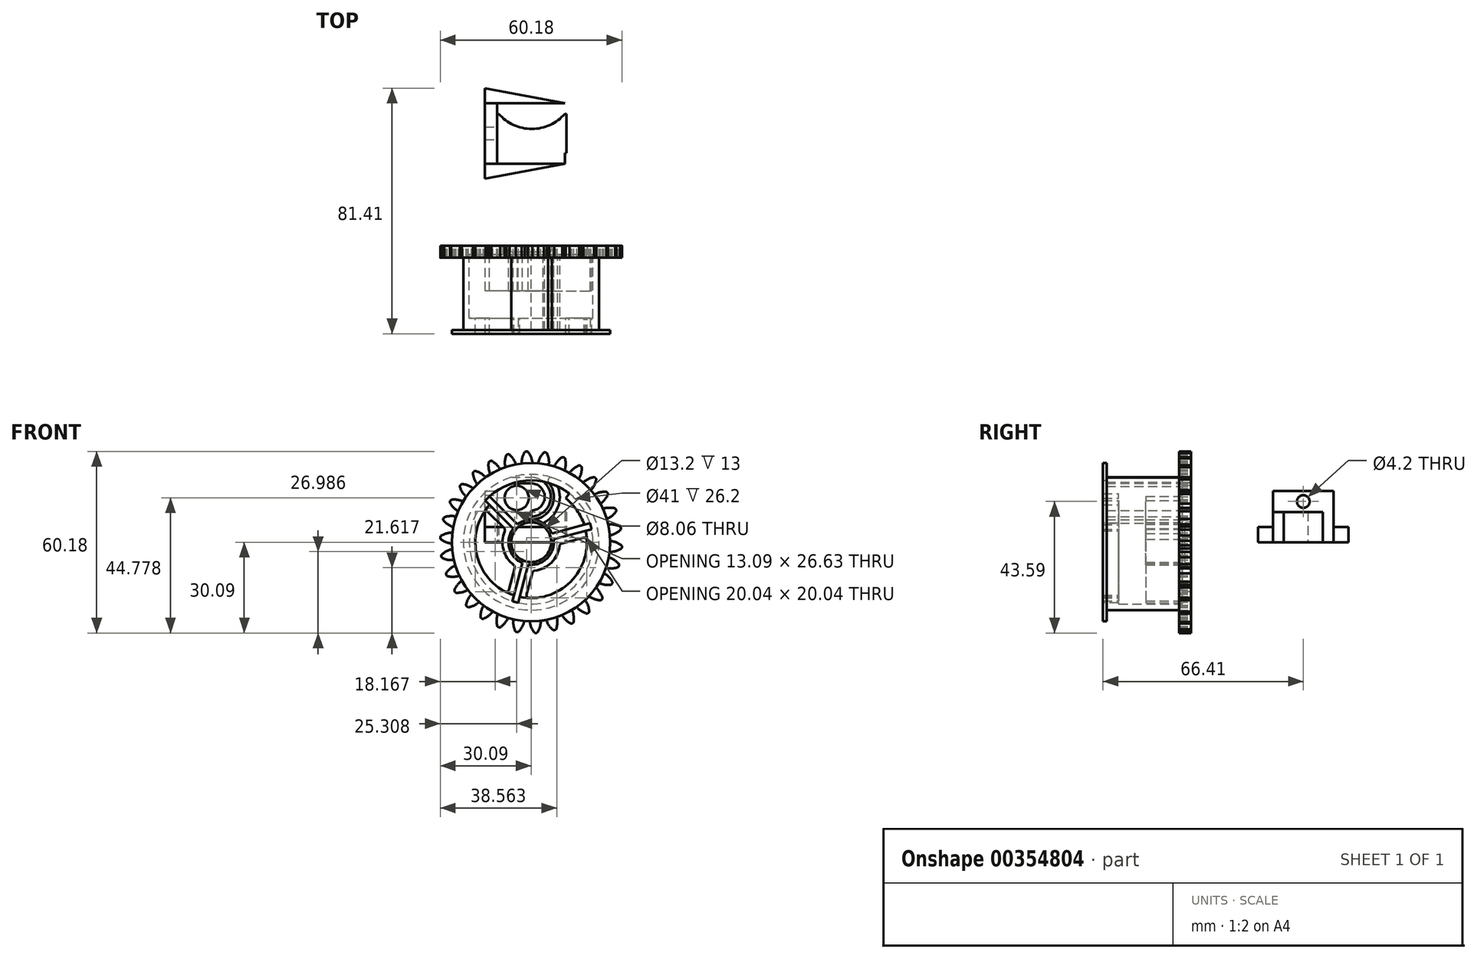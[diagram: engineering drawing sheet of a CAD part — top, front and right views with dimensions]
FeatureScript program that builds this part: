
annotation { "Feature Type Name" : "Feature", "Feature Type Description" : "" }
export const myFeature = defineFeature(function(context is Context, id is Id, definition is map)
    precondition{}
    {
        {
            var Q0;
            Q0=qCreatedBy(makeId("Front.planeOp"),FACE);
            var sketch = newSketch(context, id + "F0", { "sketchPlane" : qUnion([Q0])});
            skCircle(sketch, "E0", {"center": v(0, 0) * mm, "radius": 26.25 * mm});
            skCircle(sketch, "E1", {"center": v(0, 0) * mm, "radius": 30 * mm, "construction": true});
            skCircle(sketch, "E2", {"center": v(0, 0) * mm, "radius": 28.12 * mm, "construction": true});
            skLineSegment(sketch, "E3", {"start": v(0, 0) * mm, "end": v(0, 53.52) * mm, "construction": true});
            skLineSegment(sketch, "E4", {"start": v(0, 0) * mm, "end": v(-2.07, 39.41) * mm, "construction": true});
            skLineSegment(sketch, "E5", {"start": v(0, 28.12) * mm, "end": v(-31.73, 28.12) * mm, "construction": true});
            skLineSegment(sketch, "E6", {"start": v(0, 28.13) * mm, "end": v(-33.86, 15.8) * mm, "construction": true});
            skCircle(sketch, "E7", {"center": v(0, 28.12) * mm, "radius": 7.03 * mm, "construction": true});
            skCircle(sketch, "E8", {"center": v(0, 0) * mm, "radius": 26.43 * mm, "construction": true});
            skCircle(sketch, "E9", {"center": v(-6.56, 25.6) * mm, "radius": 7.03 * mm, "construction": true});
            skArc(sketch, "E10", {"start": v(0.44, 26.25) * mm, "mid": v(-0.04, 28.22) * mm, "end": v(-1.06, 29.98) * mm});
            skCircle(sketch, "E11.MirrorC", {"center": v(3.85, 26.15) * mm, "radius": 7.03 * mm, "construction": true});
            skArc(sketch, "E12.MirrorCS", {"start": v(-3.18, 26.06) * mm, "mid": v(-2.91, 28.07) * mm, "end": v(-2.08, 29.93) * mm});
            skArc(sketch, "E13", {"start": v(-1.06, 29.98) * mm, "mid": v(-1.58, 30.1) * mm, "end": v(-2.08, 29.93) * mm});
            skCircle(sketch, "E14", {"center": v(0, 0) * mm, "radius": 6.6 * mm});
            skCircle(sketch, "E15", {"center": v(0, 0) * mm, "radius": 7.5 * mm});
            skCircle(sketch, "E16", {"center": v(0, 0) * mm, "radius": 22.5 * mm});
            skCircle(sketch, "E17", {"center": v(0, 0) * mm, "radius": 20.5 * mm});
            skArc(sketch, "E18", {"start": v(0, 7.5) * mm, "mid": v(7.5, 15) * mm, "end": v(0, 22.5) * mm});
            skArc(sketch, "E19.0", {"start": v(0, 8.5) * mm, "mid": v(6.5, 15) * mm, "end": v(0, 21.5) * mm});
            skArc(sketch, "E20.0", {"start": v(0, 5.5) * mm, "mid": v(9.5, 15) * mm, "end": v(0, 24.5) * mm});
            skArc(sketch, "E21.0", {"start": v(0, 10.5) * mm, "mid": v(4.5, 15) * mm, "end": v(0, 19.5) * mm});
            skLineSegment(sketch, "E22", {"start": v(0, 19.5) * mm, "end": v(-6.32, 19.5) * mm});
            skLineSegment(sketch, "E23", {"start": v(0, 21.5) * mm, "end": v(-6.63, 21.5) * mm});
            skLineSegment(sketch, "E24", {"start": v(0, 10.5) * mm, "end": v(0, 8.5) * mm});
            skCircle(sketch, "E25", {"center": v(0, 0) * mm, "radius": 10 * mm});
            skLineSegment(sketch, "E26", {"start": v(-5.3, 5.3) * mm, "end": v(-14.5, 14.5) * mm, "construction": true});
            skLineSegment(sketch, "E27.0", {"start": v(-4.55, 5.96) * mm, "end": v(-13.79, 15.2) * mm});
            skLineSegment(sketch, "E28.0", {"start": v(-5.96, 4.55) * mm, "end": v(-15.2, 13.79) * mm});
            skLineSegment(sketch, "E29.1.0", {"start": v(-2.89, -6.92) * mm, "end": v(-6.27, -19.54) * mm});
            skLineSegment(sketch, "E29.1.1", {"start": v(-0.96, -7.44) * mm, "end": v(-4.34, -20.06) * mm});
            skLineSegment(sketch, "E29.2.0", {"start": v(7.44, 0.96) * mm, "end": v(20.06, 4.34) * mm});
            skLineSegment(sketch, "E29.2.1", {"start": v(6.92, 2.89) * mm, "end": v(19.54, 6.27) * mm});
            skPoint(sketch, "E30.orphan", {"position": v(-4.6, 6.01) * mm});
            skPoint(sketch, "E31.orphan", {"position": v(-6.01, 4.6) * mm});
            skPoint(sketch, "E32.orphan", {"position": v(-2.9, -6.99) * mm});
            skPoint(sketch, "E33.orphan", {"position": v(-0.98, -7.5) * mm});
            skPoint(sketch, "E34.orphan", {"position": v(7.5, 0.98) * mm});
            skPoint(sketch, "E35.orphan", {"position": v(6.99, 2.9) * mm});
            skArc(sketch, "E36", {"start": v(7.05, 21.37) * mm, "mid": v(5.74, 21) * mm, "end": v(5.9, 19.63) * mm});
            skSolve(sketch);
        }
        {
            var Q0;
            {var subQ0=sQuery(id+"F0.wireOp",EDGE,"E10");Q0=makeQuery(id+"F0.imprint","IMPRINT",FACE,{"disambiguationData":[TD([[makeQuery(id+"F0.imprint","IMPRINT",EDGE,{"derivedFrom":subQ0}),1.0]])]});}
            var Q1;
            {var subQ4=sQuery(id+"F0.wireOp",EDGE,"E0");var subQ5=makeQuery(id+"F0.imprint","INTERSECT",VERTEX,{"derivedFrom":[subQ4,sQuery(id+"F0.wireOp",EDGE,"E10")]});Q1=makeQuery(id+"F0.imprint","IMPRINT",FACE,{"disambiguationData":[TD([[makeQuery(id+"F0.imprint","IMPRINT",EDGE,{"disambiguationData":[TD([[subQ5,-1.0]])],"derivedFrom":subQ4}),1.0]])]});}
            extrude(context, id + "F1", {"entities" : qUnion([Q0, Q1]), "depth" : 4 * mm});
        }
        {
            var Q0;
            Q0=makeQuery(id+"F1.opExtrude","SWEPT_BODY",BODY,{"disambiguationData":[OSD([sQuery(id+"F0.wireOp",EDGE,"E0"),sQuery(id+"F0.wireOp",EDGE,"E10"),sQuery(id+"F0.wireOp",EDGE,"E12.MirrorCS"),sQuery(id+"F0.wireOp",EDGE,"E13")])]});
            var Q1;
            Q1=makeQuery(id+"F1.opExtrude","SWEPT_FACE",FACE,{"disambiguationData":[OSD([sQuery(id+"F0.wireOp",EDGE,"E0")])]});
            circularPattern(context, id + "F2", {"operationType" : NewBodyOperationType.ADD, "entities" : qUnion([Q0]), "axis" : qUnion([Q1]), "angle" : 360 * degree, "instanceCount" : 30, "equalSpace" : true});
        }
        {
            var Q0;
            {var subQ7=sQuery(id+"F0.wireOp",EDGE,"E23");Q0=makeQuery(id+"F0.imprint","IMPRINT",FACE,{"disambiguationData":[TD([[makeQuery(id+"F0.imprint","IMPRINT",EDGE,{"derivedFrom":subQ7}),1.0]])]});}
            var Q1;
            {var subQ0=sQuery(id+"F0.wireOp",EDGE,"E23");Q1=makeQuery(id+"F0.imprint","IMPRINT",FACE,{"disambiguationData":[TD([[makeQuery(id+"F0.imprint","IMPRINT",EDGE,{"derivedFrom":subQ0}),-1.0]])]});}
            var Q2;
            {var subQ0=sQuery(id+"F0.wireOp",EDGE,"E18");var subQ1=sQuery(id+"F0.wireOp",EDGE,"E16");var subQ2=makeQuery(id+"F0.imprint","INTERSECT",VERTEX,{"derivedFrom":[subQ1,subQ0]});Q2=makeQuery(id+"F0.imprint","IMPRINT",FACE,{"disambiguationData":[TD([[makeQuery(id+"F0.imprint","IMPRINT",EDGE,{"disambiguationData":[TD([[subQ2,1.0]])],"derivedFrom":subQ1}),1.0]])]});}
            var Q3;
            {var subQ0=sQuery(id+"F0.wireOp",EDGE,"E20.0");var subQ1=sQuery(id+"F0.wireOp",EDGE,"E17");var subQ2=makeQuery(id+"F0.imprint","INTERSECT",VERTEX,{"derivedFrom":[subQ1,subQ0]});Q3=makeQuery(id+"F0.imprint","IMPRINT",FACE,{"disambiguationData":[TD([[makeQuery(id+"F0.imprint","IMPRINT",EDGE,{"disambiguationData":[TD([[subQ2,-1.0]])],"derivedFrom":subQ1}),1.0]])]});}
            var Q4;
            {var subQ0=sQuery(id+"F0.wireOp",EDGE,"E18");var subQ1=sQuery(id+"F0.wireOp",EDGE,"E17");var subQ2=makeQuery(id+"F0.imprint","INTERSECT",VERTEX,{"derivedFrom":[subQ1,subQ0]});Q4=makeQuery(id+"F0.imprint","IMPRINT",FACE,{"disambiguationData":[TD([[makeQuery(id+"F0.imprint","IMPRINT",EDGE,{"disambiguationData":[TD([[subQ2,-1.0]])],"derivedFrom":subQ1}),1.0]])]});}
            var Q5;
            {var subQ1=sQuery(id+"F0.wireOp",EDGE,"E21.0");Q5=makeQuery(id+"F0.imprint","IMPRINT",FACE,{"disambiguationData":[TD([[makeQuery(id+"F0.imprint","IMPRINT",EDGE,{"derivedFrom":subQ1}),-1.0]])]});}
            var Q6;
            {var subQ1=sQuery(id+"F0.wireOp",EDGE,"E21.0");Q6=makeQuery(id+"F0.imprint","IMPRINT",FACE,{"disambiguationData":[TD([[makeQuery(id+"F0.imprint","IMPRINT",EDGE,{"derivedFrom":subQ1}),1.0]])]});}
            var Q7;
            {var subQ0=sQuery(id+"F0.wireOp",EDGE,"E28.0");var subQ1=sQuery(id+"F0.wireOp",EDGE,"E17");var subQ2=makeQuery(id+"F0.imprint","INTERSECT",VERTEX,{"derivedFrom":[subQ1,subQ0]});Q7=makeQuery(id+"F0.imprint","IMPRINT",FACE,{"disambiguationData":[TD([[makeQuery(id+"F0.imprint","IMPRINT",EDGE,{"disambiguationData":[TD([[subQ2,-1.0]])],"derivedFrom":subQ1}),1.0]])]});}
            var Q8;
            {var subQ10=sQuery(id+"F0.wireOp",EDGE,"E18");var subQ11=sQuery(id+"F0.wireOp",EDGE,"E15");var subQ12=makeQuery(id+"F0.imprint","INTERSECT",VERTEX,{"derivedFrom":[subQ11,subQ10]});Q8=makeQuery(id+"F0.imprint","IMPRINT",FACE,{"disambiguationData":[TD([[makeQuery(id+"F0.imprint","IMPRINT",EDGE,{"disambiguationData":[TD([[subQ12,-1.0]])],"derivedFrom":subQ11}),-1.0]])]});}
            var Q9;
            {var subQ0=sQuery(id+"F0.wireOp",EDGE,"E29.2.0");var subQ1=sQuery(id+"F0.wireOp",EDGE,"E17");var subQ2=makeQuery(id+"F0.imprint","INTERSECT",VERTEX,{"derivedFrom":[subQ1,subQ0]});Q9=makeQuery(id+"F0.imprint","IMPRINT",FACE,{"disambiguationData":[TD([[makeQuery(id+"F0.imprint","IMPRINT",EDGE,{"disambiguationData":[TD([[subQ2,1.0]])],"derivedFrom":subQ1}),1.0]])]});}
            var Q10;
            {var subQ0=sQuery(id+"F0.wireOp",EDGE,"E29.2.1");var subQ1=sQuery(id+"F0.wireOp",EDGE,"E17");var subQ2=makeQuery(id+"F0.imprint","INTERSECT",VERTEX,{"derivedFrom":[subQ1,subQ0]});Q10=makeQuery(id+"F0.imprint","IMPRINT",FACE,{"disambiguationData":[TD([[makeQuery(id+"F0.imprint","IMPRINT",EDGE,{"disambiguationData":[TD([[subQ2,-1.0]])],"derivedFrom":subQ1}),1.0]])]});}
            var Q11;
            {var subQ0=sQuery(id+"F0.wireOp",EDGE,"E29.2.1");var subQ1=sQuery(id+"F0.wireOp",EDGE,"E17");var subQ2=makeQuery(id+"F0.imprint","INTERSECT",VERTEX,{"derivedFrom":[subQ1,subQ0]});Q11=makeQuery(id+"F0.imprint","IMPRINT",FACE,{"disambiguationData":[TD([[makeQuery(id+"F0.imprint","IMPRINT",EDGE,{"disambiguationData":[TD([[subQ2,1.0]])],"derivedFrom":subQ1}),1.0]])]});}
            var Q12;
            {var subQ0=sQuery(id+"F0.wireOp",EDGE,"E18");var subQ1=sQuery(id+"F0.wireOp",EDGE,"E15");var subQ2=makeQuery(id+"F0.imprint","INTERSECT",VERTEX,{"derivedFrom":[subQ1,subQ0]});Q12=makeQuery(id+"F0.imprint","IMPRINT",FACE,{"disambiguationData":[TD([[makeQuery(id+"F0.imprint","IMPRINT",EDGE,{"disambiguationData":[TD([[subQ2,1.0]])],"derivedFrom":subQ1}),-1.0]])]});}
            var Q13;
            Q13=makeQuery(id+"F0.imprint","IMPRINT",FACE,{"disambiguationData":[TD([[makeQuery(id+"F0.imprint","IMPRINT",EDGE,{"derivedFrom":sQuery(id+"F0.wireOp",EDGE,"E14")}),-1.0]])]});
            var Q14;
            {var subQ0=sQuery(id+"F0.wireOp",EDGE,"E24");var subQ1=sQuery(id+"F0.wireOp",EDGE,"E19.0");var subQ2=makeQuery(id+"F0.imprint","INTERSECT",VERTEX,{"derivedFrom":[subQ1,subQ0]});Q14=makeQuery(id+"F0.imprint","IMPRINT",FACE,{"disambiguationData":[TD([[makeQuery(id+"F0.imprint","IMPRINT",EDGE,{"disambiguationData":[TD([[subQ2,-1.0]])],"derivedFrom":subQ1}),1.0]])]});}
            var Q15;
            {var subQ0=sQuery(id+"F0.wireOp",EDGE,"E29.1.0");var subQ1=sQuery(id+"F0.wireOp",EDGE,"E17");var subQ2=makeQuery(id+"F0.imprint","INTERSECT",VERTEX,{"derivedFrom":[subQ1,subQ0]});Q15=makeQuery(id+"F0.imprint","IMPRINT",FACE,{"disambiguationData":[TD([[makeQuery(id+"F0.imprint","IMPRINT",EDGE,{"disambiguationData":[TD([[subQ2,-1.0]])],"derivedFrom":subQ1}),1.0]])]});}
            var Q16;
            {var subQ0=sQuery(id+"F0.wireOp",EDGE,"E27.0");var subQ1=sQuery(id+"F0.wireOp",EDGE,"E17");var subQ2=makeQuery(id+"F0.imprint","INTERSECT",VERTEX,{"derivedFrom":[subQ1,subQ0]});Q16=makeQuery(id+"F0.imprint","IMPRINT",FACE,{"disambiguationData":[TD([[makeQuery(id+"F0.imprint","IMPRINT",EDGE,{"disambiguationData":[TD([[subQ2,-1.0]])],"derivedFrom":subQ1}),1.0]])]});}
            var Q17;
            {var subQ0=sQuery(id+"F0.wireOp",EDGE,"E29.1.0");var subQ1=sQuery(id+"F0.wireOp",EDGE,"E15");var subQ2=makeQuery(id+"F0.imprint","INTERSECT",VERTEX,{"derivedFrom":[subQ1,subQ0]});Q17=makeQuery(id+"F0.imprint","IMPRINT",FACE,{"disambiguationData":[TD([[makeQuery(id+"F0.imprint","IMPRINT",EDGE,{"disambiguationData":[TD([[subQ2,-1.0]])],"derivedFrom":subQ1}),-1.0]])]});}
            var Q18;
            {var subQ0=sQuery(id+"F0.wireOp",EDGE,"E28.0");var subQ1=sQuery(id+"F0.wireOp",EDGE,"E15");var subQ2=makeQuery(id+"F0.imprint","INTERSECT",VERTEX,{"derivedFrom":[subQ1,subQ0]});Q18=makeQuery(id+"F0.imprint","IMPRINT",FACE,{"disambiguationData":[TD([[makeQuery(id+"F0.imprint","IMPRINT",EDGE,{"disambiguationData":[TD([[subQ2,-1.0]])],"derivedFrom":subQ1}),-1.0]])]});}
            var Q19;
            {var subQ0=sQuery(id+"F0.wireOp",EDGE,"E29.1.1");var subQ1=sQuery(id+"F0.wireOp",EDGE,"E15");var subQ2=makeQuery(id+"F0.imprint","INTERSECT",VERTEX,{"derivedFrom":[subQ1,subQ0]});Q19=makeQuery(id+"F0.imprint","IMPRINT",FACE,{"disambiguationData":[TD([[makeQuery(id+"F0.imprint","IMPRINT",EDGE,{"disambiguationData":[TD([[subQ2,-1.0]])],"derivedFrom":subQ1}),-1.0]])]});}
            var Q20;
            {var subQ0=sQuery(id+"F0.wireOp",EDGE,"E27.0");var subQ1=sQuery(id+"F0.wireOp",EDGE,"E15");var subQ2=makeQuery(id+"F0.imprint","INTERSECT",VERTEX,{"derivedFrom":[subQ1,subQ0]});Q20=makeQuery(id+"F0.imprint","IMPRINT",FACE,{"disambiguationData":[TD([[makeQuery(id+"F0.imprint","IMPRINT",EDGE,{"disambiguationData":[TD([[subQ2,-1.0]])],"derivedFrom":subQ1}),-1.0]])]});}
            var Q21;
            {var subQ0=sQuery(id+"F0.wireOp",EDGE,"E29.2.1");var subQ1=sQuery(id+"F0.wireOp",EDGE,"E15");var subQ2=makeQuery(id+"F0.imprint","INTERSECT",VERTEX,{"derivedFrom":[subQ1,subQ0]});Q21=makeQuery(id+"F0.imprint","IMPRINT",FACE,{"disambiguationData":[TD([[makeQuery(id+"F0.imprint","IMPRINT",EDGE,{"disambiguationData":[TD([[subQ2,-1.0]])],"derivedFrom":subQ1}),-1.0]])]});}
            var Q22;
            {var subQ0=sQuery(id+"F0.wireOp",EDGE,"E29.2.0");var subQ1=sQuery(id+"F0.wireOp",EDGE,"E15");var subQ2=makeQuery(id+"F0.imprint","INTERSECT",VERTEX,{"derivedFrom":[subQ1,subQ0]});Q22=makeQuery(id+"F0.imprint","IMPRINT",FACE,{"disambiguationData":[TD([[makeQuery(id+"F0.imprint","IMPRINT",EDGE,{"disambiguationData":[TD([[subQ2,-1.0]])],"derivedFrom":subQ1}),-1.0]])]});}
            var Q23;
            {var subQ0=sQuery(id+"F0.wireOp",EDGE,"E36");var subQ2=sQuery(id+"F0.wireOp",EDGE,"E16");var subQ9=makeQuery(id+"F0.imprint","INTERSECT",VERTEX,{"derivedFrom":[subQ2,subQ0]});Q23=makeQuery(id+"F0.imprint","IMPRINT",FACE,{"disambiguationData":[TD([[makeQuery(id+"F0.imprint","IMPRINT",EDGE,{"disambiguationData":[TD([[subQ9,-1.0]])],"derivedFrom":subQ0}),1.0]])]});}
            extrude(context, id + "F3", {"entities" : qUnion([Q0, Q1, Q2, Q3, Q4, Q5, Q6, Q7, Q8, Q9, Q10, Q11, Q12, Q13, Q14, Q15, Q16, Q17, Q18, Q19, Q20, Q21, Q22, Q23]), "operationType" : NewBodyOperationType.ADD, "depth" : 3 * mm});
        }
        {
            var Q0;
            {var subQ7=sQuery(id+"F0.wireOp",EDGE,"E23");Q0=makeQuery(id+"F0.imprint","IMPRINT",FACE,{"disambiguationData":[TD([[makeQuery(id+"F0.imprint","IMPRINT",EDGE,{"derivedFrom":subQ7}),1.0]])]});}
            var Q1;
            {var subQ1=sQuery(id+"F0.wireOp",EDGE,"E21.0");Q1=makeQuery(id+"F0.imprint","IMPRINT",FACE,{"disambiguationData":[TD([[makeQuery(id+"F0.imprint","IMPRINT",EDGE,{"derivedFrom":subQ1}),-1.0]])]});}
            var Q2;
            {var subQ0=sQuery(id+"F0.wireOp",EDGE,"E20.0");var subQ1=sQuery(id+"F0.wireOp",EDGE,"E17");var subQ2=makeQuery(id+"F0.imprint","INTERSECT",VERTEX,{"derivedFrom":[subQ1,subQ0]});Q2=makeQuery(id+"F0.imprint","IMPRINT",FACE,{"disambiguationData":[TD([[makeQuery(id+"F0.imprint","IMPRINT",EDGE,{"disambiguationData":[TD([[subQ2,-1.0]])],"derivedFrom":subQ1}),1.0]])]});}
            var Q3;
            {var subQ0=sQuery(id+"F0.wireOp",EDGE,"E18");var subQ1=sQuery(id+"F0.wireOp",EDGE,"E15");var subQ2=makeQuery(id+"F0.imprint","INTERSECT",VERTEX,{"derivedFrom":[subQ1,subQ0]});Q3=makeQuery(id+"F0.imprint","IMPRINT",FACE,{"disambiguationData":[TD([[makeQuery(id+"F0.imprint","IMPRINT",EDGE,{"disambiguationData":[TD([[subQ2,1.0]])],"derivedFrom":subQ1}),-1.0]])]});}
            var Q4;
            {var subQ0=sQuery(id+"F0.wireOp",EDGE,"E24");var subQ1=sQuery(id+"F0.wireOp",EDGE,"E19.0");var subQ2=makeQuery(id+"F0.imprint","INTERSECT",VERTEX,{"derivedFrom":[subQ1,subQ0]});Q4=makeQuery(id+"F0.imprint","IMPRINT",FACE,{"disambiguationData":[TD([[makeQuery(id+"F0.imprint","IMPRINT",EDGE,{"disambiguationData":[TD([[subQ2,-1.0]])],"derivedFrom":subQ1}),1.0]])]});}
            var Q5;
            {var subQ0=sQuery(id+"F0.wireOp",EDGE,"E36");var subQ2=sQuery(id+"F0.wireOp",EDGE,"E16");var subQ9=makeQuery(id+"F0.imprint","INTERSECT",VERTEX,{"derivedFrom":[subQ2,subQ0]});Q5=makeQuery(id+"F0.imprint","IMPRINT",FACE,{"disambiguationData":[TD([[makeQuery(id+"F0.imprint","IMPRINT",EDGE,{"disambiguationData":[TD([[subQ9,-1.0]])],"derivedFrom":subQ0}),1.0]])]});}
            extrude(context, id + "F4", {"entities" : qUnion([Q0, Q1, Q2, Q3, Q4, Q5]), "operationType" : NewBodyOperationType.ADD, "depth" : 28 * mm});
        }
        {
            var Q0;
            {var subQ0=sQuery(id+"F0.wireOp",EDGE,"E29.2.1");var subQ1=sQuery(id+"F0.wireOp",EDGE,"E17");var subQ2=makeQuery(id+"F0.imprint","INTERSECT",VERTEX,{"derivedFrom":[subQ1,subQ0]});Q0=makeQuery(id+"F0.imprint","IMPRINT",FACE,{"disambiguationData":[TD([[makeQuery(id+"F0.imprint","IMPRINT",EDGE,{"disambiguationData":[TD([[subQ2,1.0]])],"derivedFrom":subQ1}),1.0]])]});}
            var Q1;
            {var subQ0=sQuery(id+"F0.wireOp",EDGE,"E29.2.0");var subQ1=sQuery(id+"F0.wireOp",EDGE,"E15");var subQ2=makeQuery(id+"F0.imprint","INTERSECT",VERTEX,{"derivedFrom":[subQ1,subQ0]});Q1=makeQuery(id+"F0.imprint","IMPRINT",FACE,{"disambiguationData":[TD([[makeQuery(id+"F0.imprint","IMPRINT",EDGE,{"disambiguationData":[TD([[subQ2,-1.0]])],"derivedFrom":subQ1}),-1.0]])]});}
            var Q2;
            Q2=makeQuery(id+"F0.imprint","IMPRINT",FACE,{"disambiguationData":[TD([[makeQuery(id+"F0.imprint","IMPRINT",EDGE,{"derivedFrom":sQuery(id+"F0.wireOp",EDGE,"E14")}),-1.0]])]});
            var Q3;
            {var subQ0=sQuery(id+"F0.wireOp",EDGE,"E29.1.0");var subQ1=sQuery(id+"F0.wireOp",EDGE,"E15");var subQ2=makeQuery(id+"F0.imprint","INTERSECT",VERTEX,{"derivedFrom":[subQ1,subQ0]});Q3=makeQuery(id+"F0.imprint","IMPRINT",FACE,{"disambiguationData":[TD([[makeQuery(id+"F0.imprint","IMPRINT",EDGE,{"disambiguationData":[TD([[subQ2,-1.0]])],"derivedFrom":subQ1}),-1.0]])]});}
            var Q4;
            {var subQ0=sQuery(id+"F0.wireOp",EDGE,"E29.1.0");var subQ1=sQuery(id+"F0.wireOp",EDGE,"E17");var subQ2=makeQuery(id+"F0.imprint","INTERSECT",VERTEX,{"derivedFrom":[subQ1,subQ0]});Q4=makeQuery(id+"F0.imprint","IMPRINT",FACE,{"disambiguationData":[TD([[makeQuery(id+"F0.imprint","IMPRINT",EDGE,{"disambiguationData":[TD([[subQ2,-1.0]])],"derivedFrom":subQ1}),1.0]])]});}
            var Q5;
            {var subQ0=sQuery(id+"F0.wireOp",EDGE,"E27.0");var subQ1=sQuery(id+"F0.wireOp",EDGE,"E17");var subQ2=makeQuery(id+"F0.imprint","INTERSECT",VERTEX,{"derivedFrom":[subQ1,subQ0]});Q5=makeQuery(id+"F0.imprint","IMPRINT",FACE,{"disambiguationData":[TD([[makeQuery(id+"F0.imprint","IMPRINT",EDGE,{"disambiguationData":[TD([[subQ2,-1.0]])],"derivedFrom":subQ1}),1.0]])]});}
            var Q6;
            {var subQ0=sQuery(id+"F0.wireOp",EDGE,"E27.0");var subQ1=sQuery(id+"F0.wireOp",EDGE,"E15");var subQ2=makeQuery(id+"F0.imprint","INTERSECT",VERTEX,{"derivedFrom":[subQ1,subQ0]});Q6=makeQuery(id+"F0.imprint","IMPRINT",FACE,{"disambiguationData":[TD([[makeQuery(id+"F0.imprint","IMPRINT",EDGE,{"disambiguationData":[TD([[subQ2,-1.0]])],"derivedFrom":subQ1}),-1.0]])]});}
            extrude(context, id + "F5", {"entities" : qUnion([Q0, Q1, Q2, Q3, Q4, Q5, Q6]), "operationType" : NewBodyOperationType.ADD, "depth" : 15 * mm});
        }
        {
            var Q0;
            {var subQ0=sQuery(id+"F0.wireOp",EDGE,"E28.0");Q0=makeQuery(id+"F5.boolean.opBoolean","SPLIT",FACE,{"disambiguationData":[TD([makeQuery(id+"F5.opExtrude","SWEPT_FACE",FACE,{"disambiguationData":[OSD([subQ0])]})])],"derivedFrom":makeQuery(id+"F3.opExtrude","CAP_FACE",FACE,{"disambiguationData":[OSD([sQuery(id+"F0.wireOp",EDGE,"E14"),sQuery(id+"F0.wireOp",EDGE,"E16"),sQuery(id+"F0.wireOp",EDGE,"E18"),sQuery(id+"F0.wireOp",EDGE,"E36")])],"isStart":false})});}
            var sketch = newSketch(context, id + "F6", { "sketchPlane" : qUnion([Q0])});
            skLineSegment(sketch, "E37.1.0", {"start": v(-0.96, -7.44) * mm, "end": v(-4.33, -20.04) * mm});
            skArc(sketch, "E37.1.1", {"start": v(20.04, 4.33) * mm, "mid": v(14.5, -14.5) * mm, "end": v(-4.33, -20.04) * mm});
            skLineSegment(sketch, "E37.1.2", {"start": v(20.04, 4.33) * mm, "end": v(7.44, 0.96) * mm});
            skArc(sketch, "E37.1.3", {"start": v(7.44, 0.96) * mm, "mid": v(5.3, -5.3) * mm, "end": v(-0.96, -7.44) * mm});
            skLineSegment(sketch, "E38.0", {"start": v(0.39, -10.15) * mm, "end": v(-1.51, -17.23) * mm});
            skArc(sketch, "E38.1", {"start": v(9.42, -1.22) * mm, "mid": v(6.72, -6.72) * mm, "end": v(1.22, -9.42) * mm});
            skLineSegment(sketch, "E38.2", {"start": v(17.23, 1.51) * mm, "end": v(10.15, -0.39) * mm});
            skArc(sketch, "E38.3", {"start": v(18.5, 0.58) * mm, "mid": v(13.08, -13.08) * mm, "end": v(-0.58, -18.5) * mm});
            skPoint(sketch, "E39.visualSharp", {"position": v(-1.83, -18.4) * mm});
            skArc(sketch, "E39.filletArc", {"start": v(-1.51, -17.23) * mm, "mid": v(-1.35, -18.09) * mm, "end": v(-0.58, -18.5) * mm});
            skPoint(sketch, "E40.visualSharp", {"position": v(0.56, -9.48) * mm});
            skArc(sketch, "E40.filletArc", {"start": v(1.22, -9.42) * mm, "mid": v(0.7, -9.66) * mm, "end": v(0.39, -10.15) * mm});
            skPoint(sketch, "E41.visualSharp", {"position": v(9.48, -0.56) * mm});
            skArc(sketch, "E41.filletArc", {"start": v(10.15, -0.39) * mm, "mid": v(9.66, -0.7) * mm, "end": v(9.42, -1.22) * mm});
            skPoint(sketch, "E42.visualSharp", {"position": v(18.4, 1.83) * mm});
            skArc(sketch, "E42.filletArc", {"start": v(18.5, 0.58) * mm, "mid": v(18.09, 1.35) * mm, "end": v(17.23, 1.51) * mm});
            skCircle(sketch, "E43", {"center": v(-4.78, 14.69) * mm, "radius": 4.03 * mm});
            skLineSegment(sketch, "E44.1.0", {"start": v(-8.99, 4.74) * mm, "end": v(-14.17, 9.93) * mm});
            skArc(sketch, "E44.1.1", {"start": v(-14.17, 9.93) * mm, "mid": v(-15, 10.21) * mm, "end": v(-15.73, 9.75) * mm});
            skArc(sketch, "E44.1.2", {"start": v(-8.75, -16.3) * mm, "mid": v(-17.87, -4.79) * mm, "end": v(-15.73, 9.75) * mm});
            skArc(sketch, "E44.1.3", {"start": v(-8.77, 3.65) * mm, "mid": v(-8.71, 4.23) * mm, "end": v(-8.99, 4.74) * mm});
            skArc(sketch, "E44.1.4", {"start": v(-5.77, -7.55) * mm, "mid": v(-9.18, -2.46) * mm, "end": v(-8.77, 3.65) * mm});
            skLineSegment(sketch, "E44.1.5", {"start": v(-7.3, -15.68) * mm, "end": v(-5.41, -8.6) * mm});
            skArc(sketch, "E44.1.6", {"start": v(-5.41, -8.6) * mm, "mid": v(-5.43, -8.02) * mm, "end": v(-5.77, -7.55) * mm});
            skArc(sketch, "E44.1.7", {"start": v(-8.75, -16.3) * mm, "mid": v(-7.88, -16.34) * mm, "end": v(-7.3, -15.68) * mm});
            skLineSegment(sketch, "E44.anchor1", {"start": v(0, 0) * mm, "end": v(-1.51, -17.23) * mm, "construction": true});
            skLineSegment(sketch, "E44.anchor2", {"start": v(0, 0) * mm, "end": v(-14.17, 9.93) * mm, "construction": true});
            skSolve(sketch);
        }
        {
            var Q0;
            Q0=makeQuery(id+"F3.opExtrude","CAP_EDGE",EDGE,{"disambiguationData":[OSD([sQuery(id+"F0.wireOp",EDGE,"E14")])],"isStart":true});
            chamfer(context, id + "F7", {"entities" : qUnion([Q0]), "chamferType" : ChamferType.TWO_OFFSETS, "width1" : 0.4 * mm, "oppositeDirection" : false, "width2" : 2 * mm, "tangentPropagation" : true});
        }
        {
            var Q0;
            Q0=makeQuery(id+"F6.imprint","IMPRINT",FACE,{"disambiguationData":[TD([[makeQuery(id+"F6.imprint","IMPRINT",EDGE,{"derivedFrom":sQuery(id+"F6.wireOp",EDGE,"E38.0")}),1.0]])]});
            var Q1;
            Q1=makeQuery(id+"F6.imprint","IMPRINT",FACE,{"disambiguationData":[TD([[makeQuery(id+"F6.imprint","IMPRINT",EDGE,{"derivedFrom":sQuery(id+"F6.wireOp",EDGE,"E44.1.0")}),1.0]])]});
            var Q2;
            Q2=makeQuery(id+"F6.imprint","IMPRINT",FACE,{"disambiguationData":[TD([[makeQuery(id+"F6.imprint","IMPRINT",EDGE,{"derivedFrom":sQuery(id+"F6.wireOp",EDGE,"E43")}),1.0]])]});
            extrude(context, id + "F8", {"entities" : qUnion([Q0, Q1, Q2]), "operationType" : NewBodyOperationType.REMOVE, "endBound" : BoundingType.UP_TO_NEXT, "oppositeDirection" : true, "depth" : 25 * mm});
        }
        {
            var Q0;
            Q0=qCreatedBy(makeId("Top.planeOp"),FACE);
            var sketch = newSketch(context, id + "F9", { "sketchPlane" : qUnion([Q0])});
            skLineSegment(sketch, "E45.bottom", {"start": v(-10.79, 35.71) * mm, "end": v(11.21, 35.71) * mm, "construction": true});
            skLineSegment(sketch, "E45.top", {"start": v(-10.79, 30.71) * mm, "end": v(11.21, 30.71) * mm, "construction": true});
            skLineSegment(sketch, "E45.left", {"start": v(-10.79, 35.71) * mm, "end": v(-10.79, 30.71) * mm, "construction": true});
            skLineSegment(sketch, "E45.right", {"start": v(11.21, 35.71) * mm, "end": v(11.21, 30.71) * mm, "construction": true});
            skArc(sketch, "E46", {"start": v(11.21, 30.71) * mm, "mid": v(0.21, 35.71) * mm, "end": v(-10.79, 30.71) * mm});
            skLineSegment(sketch, "E47.0", {"start": v(-11.29, 37.21) * mm, "end": v(10.71, 37.21) * mm, "construction": true});
            skArc(sketch, "E48.MirrorCS", {"start": v(11.21, 43.71) * mm, "mid": v(0.21, 38.71) * mm, "end": v(-10.79, 43.71) * mm});
            skLineSegment(sketch, "E49", {"start": v(-10.79, 43.71) * mm, "end": v(-11.29, 43.71) * mm, "construction": true});
            skLineSegment(sketch, "E50", {"start": v(-11.29, 43.71) * mm, "end": v(-11.29, 30.71) * mm});
            skLineSegment(sketch, "E51", {"start": v(-11.29, 30.71) * mm, "end": v(-10.79, 30.71) * mm});
            skLineSegment(sketch, "E52", {"start": v(-11.29, 43.71) * mm, "end": v(-10.79, 43.71) * mm});
            skLineSegment(sketch, "E53", {"start": v(11.21, 43.71) * mm, "end": v(11.71, 43.71) * mm});
            skLineSegment(sketch, "E54", {"start": v(11.71, 43.71) * mm, "end": v(11.71, 30.71) * mm});
            skLineSegment(sketch, "E55", {"start": v(11.71, 30.71) * mm, "end": v(11.21, 30.71) * mm});
            skLineSegment(sketch, "E56.bottom", {"start": v(-15.29, 47.21) * mm, "end": v(14.71, 47.21) * mm});
            skLineSegment(sketch, "E56.top", {"start": v(-15.29, 27.21) * mm, "end": v(14.71, 27.21) * mm});
            skLineSegment(sketch, "E56.left", {"start": v(-15.29, 47.21) * mm, "end": v(-15.29, 27.21) * mm});
            skLineSegment(sketch, "E56.right", {"start": v(14.71, 47.21) * mm, "end": v(14.71, 27.21) * mm});
            skPoint(sketch, "E56.middle", {"position": v(-0.29, 37.21) * mm});
            skLineSegment(sketch, "E57", {"start": v(11.21, 43.71) * mm, "end": v(11.21, 47.21) * mm});
            skLineSegment(sketch, "E58", {"start": v(11.21, 30.71) * mm, "end": v(11.21, 27.21) * mm});
            skArc(sketch, "E59", {"start": v(-11.29, 31.71) * mm, "mid": v(-7.68, 37.21) * mm, "end": v(-11.29, 42.71) * mm});
            skLineSegment(sketch, "E60", {"start": v(-11.29, 43.71) * mm, "end": v(-11.29, 47.21) * mm});
            skLineSegment(sketch, "E61", {"start": v(-11.29, 30.71) * mm, "end": v(-11.29, 27.21) * mm});
            skLineSegment(sketch, "E62", {"start": v(-15.29, 47.21) * mm, "end": v(-15.29, 52.21) * mm});
            skLineSegment(sketch, "E63", {"start": v(-15.29, 52.21) * mm, "end": v(11.21, 47.21) * mm});
            skLineSegment(sketch, "E64", {"start": v(-15.29, 27.21) * mm, "end": v(-15.29, 22.21) * mm});
            skLineSegment(sketch, "E65", {"start": v(-15.29, 22.21) * mm, "end": v(11.21, 27.21) * mm});
            skSolve(sketch);
        }
        {
            var Q0;
            Q0=makeQuery(id+"F9.imprint","IMPRINT",FACE,{"disambiguationData":[TD([[makeQuery(id+"F9.imprint","IMPRINT",EDGE,{"derivedFrom":sQuery(id+"F9.wireOp",EDGE,"E46")}),1.0]])]});
            var Q1;
            {var subQ0=sQuery(id+"F9.wireOp",EDGE,"E59");Q1=makeQuery(id+"F9.imprint","IMPRINT",FACE,{"disambiguationData":[TD([[makeQuery(id+"F9.imprint","IMPRINT",EDGE,{"derivedFrom":subQ0}),1.0]])]});}
            var Q2;
            Q2=makeQuery(id+"F9.imprint","IMPRINT",FACE,{"disambiguationData":[TD([[makeQuery(id+"F9.imprint","IMPRINT",EDGE,{"derivedFrom":sQuery(id+"F9.wireOp",EDGE,"E48.MirrorCS")}),-1.0]])]});
            var Q3;
            {var subQ0=sQuery(id+"F9.wireOp",EDGE,"E56.left");Q3=makeQuery(id+"F9.imprint","IMPRINT",FACE,{"disambiguationData":[TD([[makeQuery(id+"F9.imprint","IMPRINT",EDGE,{"derivedFrom":subQ0}),1.0]])]});}
            extrude(context, id + "F10", {"entities" : qUnion([Q0, Q1, Q2, Q3]), "depth" : 10 * mm});
        }
        {
            var Q0;
            {var subQ0=sQuery(id+"F9.wireOp",EDGE,"E56.left");Q0=makeQuery(id+"F9.imprint","IMPRINT",FACE,{"disambiguationData":[TD([[makeQuery(id+"F9.imprint","IMPRINT",EDGE,{"derivedFrom":subQ0}),1.0]])]});}
            extrude(context, id + "F11", {"entities" : qUnion([Q0]), "operationType" : NewBodyOperationType.ADD, "depth" : 17 * mm});
        }
        {
            var Q0;
            {var subQ0=sQuery(id+"F9.wireOp",EDGE,"E62");Q0=makeQuery(id+"F9.imprint","IMPRINT",FACE,{"disambiguationData":[TD([[makeQuery(id+"F9.imprint","IMPRINT",EDGE,{"derivedFrom":subQ0}),-1.0]])]});}
            var Q1;
            {var subQ0=sQuery(id+"F9.wireOp",EDGE,"E64");Q1=makeQuery(id+"F9.imprint","IMPRINT",FACE,{"disambiguationData":[TD([[makeQuery(id+"F9.imprint","IMPRINT",EDGE,{"derivedFrom":subQ0}),1.0]])]});}
            extrude(context, id + "F12", {"entities" : qUnion([Q0, Q1]), "operationType" : NewBodyOperationType.ADD, "depth" : 5 * mm});
        }
        {
            var Q0;
            {var subQ0=sQuery(id+"F9.wireOp",EDGE,"E61");var subQ1=sQuery(id+"F9.wireOp",EDGE,"E60");var subQ2=sQuery(id+"F9.wireOp",EDGE,"E50");var subQ3=sQuery(id+"F9.wireOp",EDGE,"E59");Q0=makeQuery(id+"F11.boolean.opBoolean","MERGE",FACE,{"derivedFrom":[makeQuery(id+"F10.opExtrude","SWEPT_FACE",FACE,{"disambiguationData":[OSD([subQ2]),TDD([makeQuery(id+"F9.imprint","IMPRINT",EDGE,{"disambiguationData":[TD([[makeQuery(id+"F9.imprint","INTERSECT",VERTEX,{"disambiguationData":[OD(1.0)],"derivedFrom":[subQ2,subQ3]}),1.0]])],"derivedFrom":subQ2})])]}),makeQuery(id+"F10.opExtrude","SWEPT_FACE",FACE,{"disambiguationData":[OSD([subQ2]),TDD([makeQuery(id+"F9.imprint","IMPRINT",EDGE,{"disambiguationData":[TD([[makeQuery(id+"F9.imprint","INTERSECT",VERTEX,{"disambiguationData":[OD(0.0)],"derivedFrom":[subQ2,subQ3]}),-1.0]])],"derivedFrom":subQ2})])]}),makeQuery(id+"F11.opExtrude","SWEPT_FACE",FACE,{"disambiguationData":[OSD([subQ2,subQ1,subQ0])]})]});}
            var sketch = newSketch(context, id + "F13", { "sketchPlane" : qUnion([Q0])});
            skCircle(sketch, "E66", {"center": v(37.21, 13.5) * mm, "radius": 2.1 * mm});
            skPoint(sketch, "E66.centerSnap0", {"position": v(27.21, 13.5) * mm});
            skPoint(sketch, "E66.centerSnap1", {"position": v(37.21, 10) * mm});
            skSolve(sketch);
        }
        {
            var Q0;
            Q0=makeQuery(id+"F13.imprint","IMPRINT",FACE,{"disambiguationData":[TD([[makeQuery(id+"F13.imprint","IMPRINT",EDGE,{"derivedFrom":sQuery(id+"F13.wireOp",EDGE,"E66")}),1.0]])]});
            extrude(context, id + "F14", {"entities" : qUnion([Q0]), "operationType" : NewBodyOperationType.REMOVE, "endBound" : BoundingType.UP_TO_NEXT, "oppositeDirection" : true, "depth" : 25 * mm});
        }
        {
            var Q0;
            Q0=makeQuery(id+"F4.opExtrude","CAP_FACE",FACE,{"disambiguationData":[OSD([sQuery(id+"F0.wireOp",EDGE,"E15"),sQuery(id+"F0.wireOp",EDGE,"E16"),sQuery(id+"F0.wireOp",EDGE,"E17"),sQuery(id+"F0.wireOp",EDGE,"E18"),sQuery(id+"F0.wireOp",EDGE,"E19.0"),sQuery(id+"F0.wireOp",EDGE,"E20.0"),sQuery(id+"F0.wireOp",EDGE,"E21.0"),sQuery(id+"F0.wireOp",EDGE,"E22"),sQuery(id+"F0.wireOp",EDGE,"E23"),sQuery(id+"F0.wireOp",EDGE,"E24"),sQuery(id+"F0.wireOp",EDGE,"E36")])],"isStart":false});
            var sketch = newSketch(context, id + "F15", { "sketchPlane" : qUnion([Q0])});
            skCircle(sketch, "E67.0", {"center": v(0, 0) * mm, "radius": 22.5 * mm});
            skCircle(sketch, "E67.1", {"center": v(0, 0) * mm, "radius": 20.5 * mm});
            skCircle(sketch, "E67.2", {"center": v(0, 0) * mm, "radius": 26.25 * mm});
            skLineSegment(sketch, "E68.0.0", {"start": v(-6.33, 7.74) * mm, "end": v(-13.77, 15.19) * mm});
            skArc(sketch, "E68.0.1", {"start": v(-13.77, 15.19) * mm, "mid": v(-14.5, 14.5) * mm, "end": v(-15.19, 13.77) * mm});
            skLineSegment(sketch, "E68.0.2", {"start": v(-15.19, 13.77) * mm, "end": v(-7.74, 6.33) * mm});
            skArc(sketch, "E68.0.3", {"start": v(-7.74, 6.33) * mm, "mid": v(-7.07, 7.07) * mm, "end": v(-6.33, 7.74) * mm});
            skLineSegment(sketch, "E68.1.0", {"start": v(19.52, 6.27) * mm, "end": v(9.35, 3.54) * mm});
            skArc(sketch, "E68.1.1", {"start": v(9.35, 3.54) * mm, "mid": v(9.66, 2.59) * mm, "end": v(9.87, 1.6) * mm});
            skLineSegment(sketch, "E68.1.2", {"start": v(9.87, 1.6) * mm, "end": v(20.04, 4.33) * mm});
            skArc(sketch, "E68.1.3", {"start": v(20.04, 4.33) * mm, "mid": v(19.8, 5.3) * mm, "end": v(19.52, 6.27) * mm});
            skLineSegment(sketch, "E68.2.0", {"start": v(-4.33, -20.04) * mm, "end": v(-1.6, -9.87) * mm});
            skArc(sketch, "E68.2.1", {"start": v(-1.6, -9.87) * mm, "mid": v(-2.59, -9.66) * mm, "end": v(-3.54, -9.35) * mm});
            skLineSegment(sketch, "E68.2.2", {"start": v(-3.54, -9.35) * mm, "end": v(-6.27, -19.52) * mm});
            skArc(sketch, "E68.2.3", {"start": v(-6.27, -19.52) * mm, "mid": v(-5.3, -19.8) * mm, "end": v(-4.33, -20.04) * mm});
            skLineSegment(sketch, "E69", {"start": v(-11.46, 10.05) * mm, "end": v(-10.05, 11.46) * mm});
            skLineSegment(sketch, "E70", {"start": v(14.44, 4.9) * mm, "end": v(14.95, 2.97) * mm});
            skLineSegment(sketch, "E71", {"start": v(-4.9, -14.44) * mm, "end": v(-2.97, -14.95) * mm});
            skCircle(sketch, "E72", {"center": v(0, 0) * mm, "radius": 18.5 * mm});
            skLineSegment(sketch, "E73", {"start": v(11.4, 14.56) * mm, "end": v(12.64, 16.14) * mm});
            skSolve(sketch);
        }
        {
            var Q0;
            Q0=makeQuery(id+"F15.imprint","IMPRINT",FACE,{"disambiguationData":[TD([[makeQuery(id+"F15.imprint","IMPRINT",EDGE,{"derivedFrom":sQuery(id+"F15.wireOp",EDGE,"E67.2")}),1.0]])]});
            var Q1;
            {var subQ11=makeQuery(id+"F4.opExtrude","CAP_EDGE",EDGE,{"disambiguationData":[OSD([sQuery(id+"F0.wireOp",EDGE,"E23")])],"isStart":false});Q1=makeQuery(id+"F15.imprint","IMPRINT",FACE,{"disambiguationData":[TD([[makeQuery(id+"F15.imprint","IMPRINT",EDGE,{"derivedFrom":subQ11}),1.0]])]});}
            var Q2;
            {var subQ0=sQuery(id+"F15.wireOp",EDGE,"E68.0.2");var subQ1=sQuery(id+"F15.wireOp",EDGE,"E67.1");var subQ2=makeQuery(id+"F15.imprint","INTERSECT",VERTEX,{"derivedFrom":[subQ1,subQ0]});Q2=makeQuery(id+"F15.imprint","IMPRINT",FACE,{"disambiguationData":[TD([[makeQuery(id+"F15.imprint","IMPRINT",EDGE,{"disambiguationData":[TD([[subQ2,-1.0]])],"derivedFrom":subQ1}),1.0]])]});}
            var Q3;
            {var subQ0=sQuery(id+"F15.wireOp",EDGE,"E68.0.0");var subQ1=sQuery(id+"F15.wireOp",EDGE,"E67.1");var subQ2=makeQuery(id+"F15.imprint","INTERSECT",VERTEX,{"derivedFrom":[subQ1,subQ0]});Q3=makeQuery(id+"F15.imprint","IMPRINT",FACE,{"disambiguationData":[TD([[makeQuery(id+"F15.imprint","IMPRINT",EDGE,{"disambiguationData":[TD([[subQ2,-1.0]])],"derivedFrom":subQ1}),1.0]])]});}
            var Q4;
            {var subQ3=sQuery(id+"F15.wireOp",EDGE,"E73");Q4=makeQuery(id+"F15.imprint","IMPRINT",FACE,{"disambiguationData":[TD([[makeQuery(id+"F15.imprint","IMPRINT",EDGE,{"derivedFrom":subQ3}),-1.0]])]});}
            var Q5;
            {var subQ0=sQuery(id+"F15.wireOp",EDGE,"E68.1.2");var subQ1=sQuery(id+"F15.wireOp",EDGE,"E67.1");var subQ2=makeQuery(id+"F15.imprint","INTERSECT",VERTEX,{"derivedFrom":[subQ1,subQ0]});Q5=makeQuery(id+"F15.imprint","IMPRINT",FACE,{"disambiguationData":[TD([[makeQuery(id+"F15.imprint","IMPRINT",EDGE,{"disambiguationData":[TD([[subQ2,1.0]])],"derivedFrom":subQ1}),1.0]])]});}
            var Q6;
            {var subQ0=makeQuery(id+"F4.opExtrude","CAP_EDGE",EDGE,{"disambiguationData":[OSD([sQuery(id+"F0.wireOp",EDGE,"E23")])],"isStart":false});Q6=makeQuery(id+"F15.imprint","IMPRINT",FACE,{"disambiguationData":[TD([[makeQuery(id+"F15.imprint","IMPRINT",EDGE,{"derivedFrom":subQ0}),-1.0]])]});}
            extrude(context, id + "F16", {"entities" : qUnion([Q0, Q1, Q2, Q3, Q4, Q5, Q6]), "depth" : 1.2 * mm});
        }
        {
            var Q0;
            {var subQ0=sQuery(id+"F15.wireOp",EDGE,"E68.0.2");var subQ1=sQuery(id+"F15.wireOp",EDGE,"E67.1");var subQ2=makeQuery(id+"F15.imprint","INTERSECT",VERTEX,{"derivedFrom":[subQ1,subQ0]});Q0=makeQuery(id+"F15.imprint","IMPRINT",FACE,{"disambiguationData":[TD([[makeQuery(id+"F15.imprint","IMPRINT",EDGE,{"disambiguationData":[TD([[subQ2,-1.0]])],"derivedFrom":subQ1}),1.0]])]});}
            var Q1;
            {var subQ0=sQuery(id+"F15.wireOp",EDGE,"E68.1.2");var subQ1=sQuery(id+"F15.wireOp",EDGE,"E67.1");var subQ2=makeQuery(id+"F15.imprint","INTERSECT",VERTEX,{"derivedFrom":[subQ1,subQ0]});Q1=makeQuery(id+"F15.imprint","IMPRINT",FACE,{"disambiguationData":[TD([[makeQuery(id+"F15.imprint","IMPRINT",EDGE,{"disambiguationData":[TD([[subQ2,1.0]])],"derivedFrom":subQ1}),1.0]])]});}
            var Q2;
            {var subQ0=sQuery(id+"F15.wireOp",EDGE,"E68.0.0");var subQ1=sQuery(id+"F15.wireOp",EDGE,"E67.1");var subQ2=makeQuery(id+"F15.imprint","INTERSECT",VERTEX,{"derivedFrom":[subQ1,subQ0]});Q2=makeQuery(id+"F15.imprint","IMPRINT",FACE,{"disambiguationData":[TD([[makeQuery(id+"F15.imprint","IMPRINT",EDGE,{"disambiguationData":[TD([[subQ2,-1.0]])],"derivedFrom":subQ1}),1.0]])]});}
            var Q3;
            {var subQ3=sQuery(id+"F15.wireOp",EDGE,"E73");Q3=makeQuery(id+"F15.imprint","IMPRINT",FACE,{"disambiguationData":[TD([[makeQuery(id+"F15.imprint","IMPRINT",EDGE,{"derivedFrom":subQ3}),-1.0]])]});}
            extrude(context, id + "F17", {"entities" : qUnion([Q0, Q1, Q2, Q3]), "operationType" : NewBodyOperationType.ADD, "oppositeDirection" : true, "depth" : 4 * mm});
        }
    });
